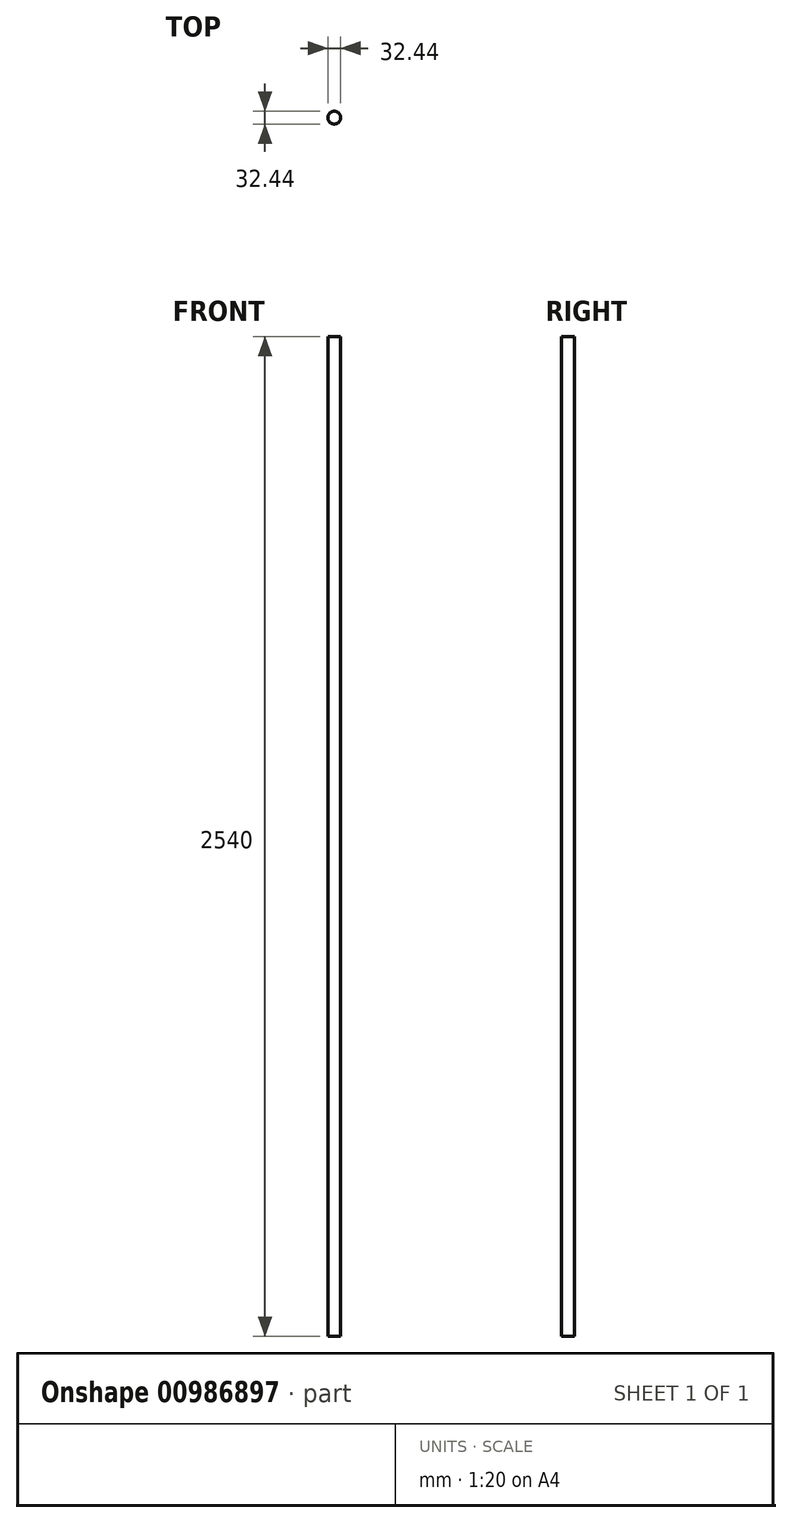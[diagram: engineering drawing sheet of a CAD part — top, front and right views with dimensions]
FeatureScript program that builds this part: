
annotation { "Feature Type Name" : "Feature", "Feature Type Description" : "" }
export const myFeature = defineFeature(function(context is Context, id is Id, definition is map)
    precondition{}
    {
        {
            var Q0;
            Q0=qCreatedBy(makeId("Top.planeOp"),FACE);
            var sketch = newSketch(context, id + "F0", { "sketchPlane" : qUnion([Q0])});
            skCircle(sketch, "E0", {"center": v(0, 0) * mm, "radius": 16.22 * mm});
            skSolve(sketch);
        }
        {
            var Q0;
            Q0=makeQuery(id+"F0.imprint","IMPRINT",FACE,{"disambiguationData":[TD([[makeQuery(id+"F0.imprint","IMPRINT",EDGE,{"derivedFrom":sQuery(id+"F0.wireOp",EDGE,"E0")}),1.0]])]});
            extrude(context, id + "F1", {"entities" : qUnion([Q0]), "depth" : 2540 * mm, "offsetDistance" : 25.4 * mm});
        }
    });
